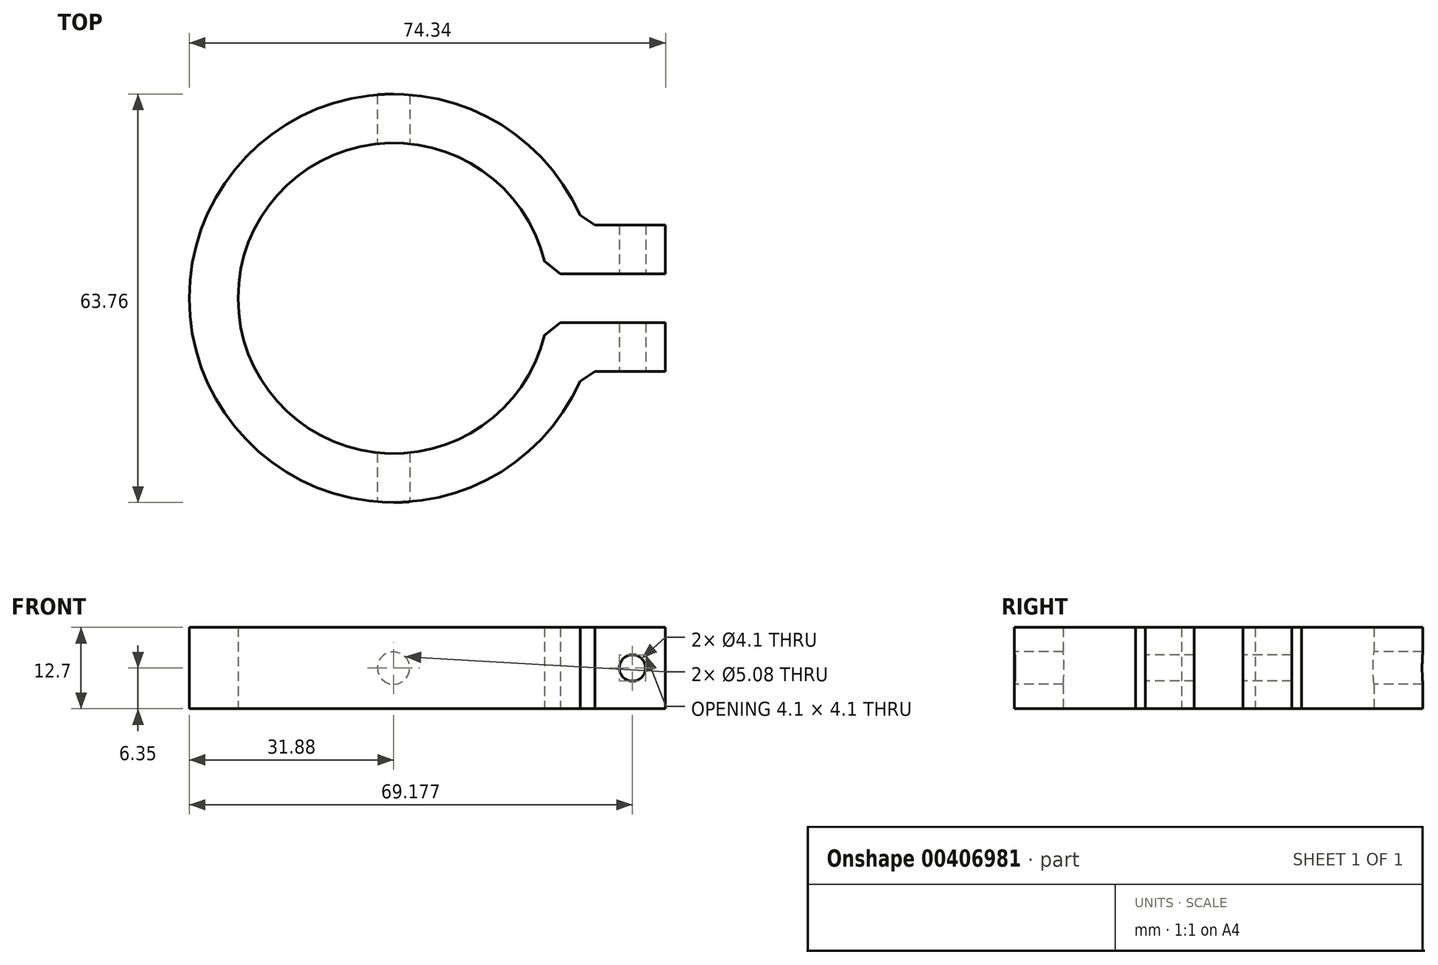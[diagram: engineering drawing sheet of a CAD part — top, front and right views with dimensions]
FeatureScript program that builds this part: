
annotation { "Feature Type Name" : "Feature", "Feature Type Description" : "" }
export const myFeature = defineFeature(function(context is Context, id is Id, definition is map)
    precondition{}
    {
        {
            var Q0;
            Q0=qCreatedBy(makeId("Top.planeOp"),FACE);
            var sketch = newSketch(context, id + "F0", { "sketchPlane" : qUnion([Q0])});
            skArc(sketch, "E0", {"start": v(23.96, 3.81) * mm, "mid": v(-24.26, 0) * mm, "end": v(23.96, -3.8) * mm});
            skArc(sketch, "E1", {"start": v(29.76, 11.43) * mm, "mid": v(-31.88, 0) * mm, "end": v(29.76, -11.43) * mm});
            skLineSegment(sketch, "E2", {"start": v(0, 0) * mm, "end": v(86.88, 0) * mm, "construction": true});
            skLineSegment(sketch, "E3", {"start": v(23.96, 3.81) * mm, "end": v(42.46, 3.81) * mm});
            skLineSegment(sketch, "E4", {"start": v(42.46, 3.81) * mm, "end": v(42.46, 11.43) * mm});
            skLineSegment(sketch, "E5", {"start": v(42.46, 11.43) * mm, "end": v(29.76, 11.43) * mm});
            skLineSegment(sketch, "E6", {"start": v(23.96, -3.8) * mm, "end": v(42.46, -3.8) * mm});
            skLineSegment(sketch, "E7", {"start": v(42.46, -3.81) * mm, "end": v(42.46, -11.43) * mm});
            skLineSegment(sketch, "E8", {"start": v(42.46, -11.43) * mm, "end": v(29.76, -11.43) * mm});
            skSolve(sketch);
        }
        {
            var Q0;
            Q0=makeQuery(id+"F0.imprint","IMPRINT",FACE,{"disambiguationData":[TD([[makeQuery(id+"F0.imprint","IMPRINT",EDGE,{"derivedFrom":sQuery(id+"F0.wireOp",EDGE,"E0")}),-1.0]])]});
            extrude(context, id + "F1", {"entities" : qUnion([Q0]), "depth" : 12.7 * mm});
        }
        {
            var Q0;
            Q0=qCreatedBy(makeId("Front.planeOp"),FACE);
            var sketch = newSketch(context, id + "F2", { "sketchPlane" : qUnion([Q0])});
            skCircle(sketch, "E9", {"center": v(0, 6.35) * mm, "radius": 2.54 * mm});
            skCircle(sketch, "E10", {"center": v(37.3, 6.35) * mm, "radius": 2.05 * mm});
            skLineSegment(sketch, "E11.0", {"start": v(42.46, 0) * mm, "end": v(29.76, 0) * mm, "construction": true});
            skLineSegment(sketch, "E12.1", {"start": v(42.46, 12.7) * mm, "end": v(29.76, 12.7) * mm, "construction": true});
            skLineSegment(sketch, "E13", {"start": v(37.3, 12.7) * mm, "end": v(37.3, 0) * mm, "construction": true});
            skSolve(sketch);
        }
        {
            var Q0;
            Q0=makeQuery(id+"F2.imprint","IMPRINT",FACE,{"disambiguationData":[TD([[makeQuery(id+"F2.imprint","IMPRINT",EDGE,{"derivedFrom":sQuery(id+"F2.wireOp",EDGE,"E9")}),1.0]])]});
            var Q1;
            Q1=makeQuery(id+"F2.imprint","IMPRINT",FACE,{"disambiguationData":[TD([[makeQuery(id+"F2.imprint","IMPRINT",EDGE,{"derivedFrom":sQuery(id+"F2.wireOp",EDGE,"E10")}),1.0]])]});
            extrude(context, id + "F3", {"entities" : qUnion([Q0, Q1]), "operationType" : NewBodyOperationType.REMOVE, "endBound" : BoundingType.THROUGH_ALL, "oppositeDirection" : true, "depth" : 25.4 * mm, "hasSecondDirection" : true, "secondDirectionBound" : SecondDirectionBoundingType.THROUGH_ALL, "secondDirectionOppositeDirection" : false, "secondDirectionDepth" : 25.4 * mm});
        }
        {
            var Q0;
            Q0=makeQuery(id+"F1.opExtrude","SWEPT_EDGE",EDGE,{"disambiguationData":[OSD([sQuery(id+"F0.wireOp",EDGE,"E1"),sQuery(id+"F0.wireOp",EDGE,"E8")])]});
            var Q1;
            Q1=makeQuery(id+"F1.opExtrude","SWEPT_EDGE",EDGE,{"disambiguationData":[OSD([sQuery(id+"F0.wireOp",EDGE,"E1"),sQuery(id+"F0.wireOp",EDGE,"E5")])]});
            var Q2;
            Q2=makeQuery(id+"F1.opExtrude","SWEPT_EDGE",EDGE,{"disambiguationData":[OSD([sQuery(id+"F0.wireOp",EDGE,"E0"),sQuery(id+"F0.wireOp",EDGE,"E6")])]});
            var Q3;
            Q3=makeQuery(id+"F1.opExtrude","SWEPT_EDGE",EDGE,{"disambiguationData":[OSD([sQuery(id+"F0.wireOp",EDGE,"E0"),sQuery(id+"F0.wireOp",EDGE,"E3")])]});
            chamfer(context, id + "F4", {"entities" : qUnion([Q0, Q1, Q2, Q3]), "width" : 2.54 * mm, "tangentPropagation" : true});
        }
    });
